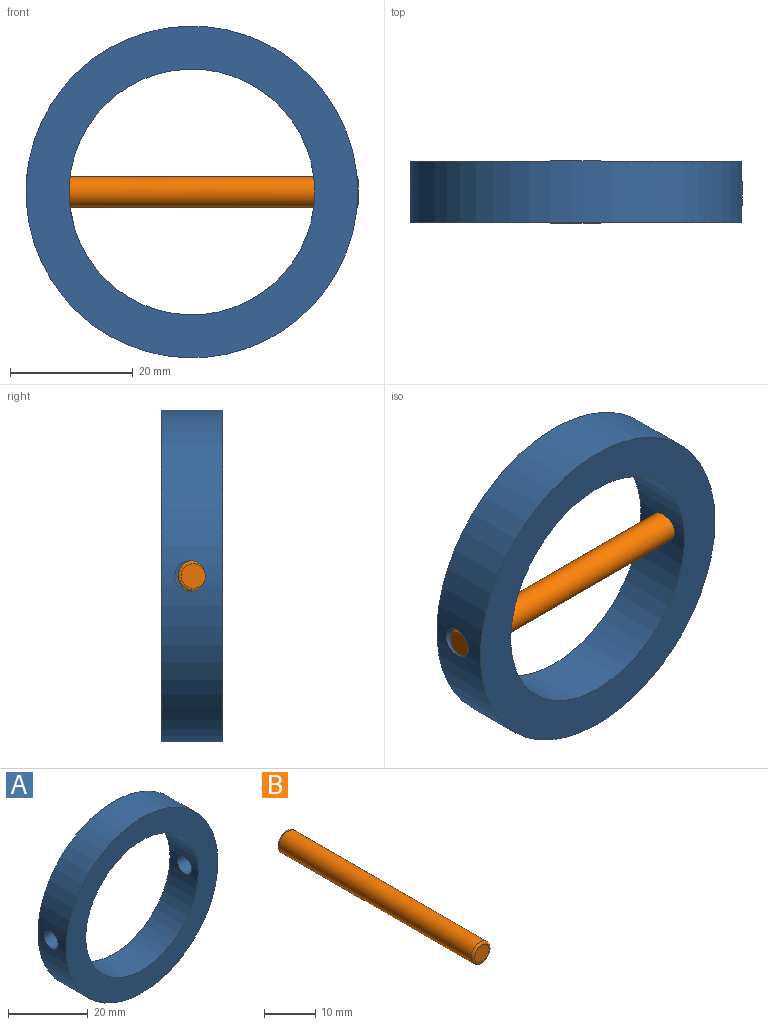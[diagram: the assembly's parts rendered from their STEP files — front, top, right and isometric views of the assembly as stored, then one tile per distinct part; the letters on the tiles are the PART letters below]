
ASSEMBLY  parts=2 mates=1
PART A: 6 faces, bbox 54x10x54 mm
  f0: cylinder r=20mm len=40mm, axis (0,1,0), area 1217.3mm2, adj f2,f3,f4,f5
  f1: cylinder r=27mm len=54mm, axis (0,1,0), area 1657.3mm2, adj f2,f3,f4,f5
  f2: plane 54x54mm, normal (0,-1,0), area 1033.8mm2, adj f0,f1
  f3: plane 54x54mm, normal (0,1,0), area 1033.8mm2, adj f0,f1
  f4: cylinder r=2.5mm len=7.16mm, axis (1,0,0), area 110.3mm2, adj f0,f1
  f5: cylinder r=2.5mm len=7.16mm, axis (-1,0,0), area 110.3mm2, adj f0,f1
PART B: 5 faces, bbox 5x54x5 mm
  f0: cylinder r=2.5mm len=53mm, axis (0,1,0), area 832.5mm2, adj f3,f4
  f1: plane 4.01x4.01mm, normal (0,-1,0), area 12.6mm2, adj f3
  f2: plane 4.01x4.01mm, normal (0,1,0), area 12.6mm2, adj f4
  f3: bspline ~5x5mm, area 11.9mm2, adj f0,f1
  f4: bspline ~5x5mm, area 11.9mm2, adj f0,f2
PLACE A t=(-13.3,-0.45,3.34)mm
PLACE B rot(axis=(0.58,-0.58,0.58),120deg) t=(-40.26,35.09,54.68)mm
MATE fastened B.f0 <-> A.f5  axis (1,0,0) through (13.74,-5.67,3.34)mm
